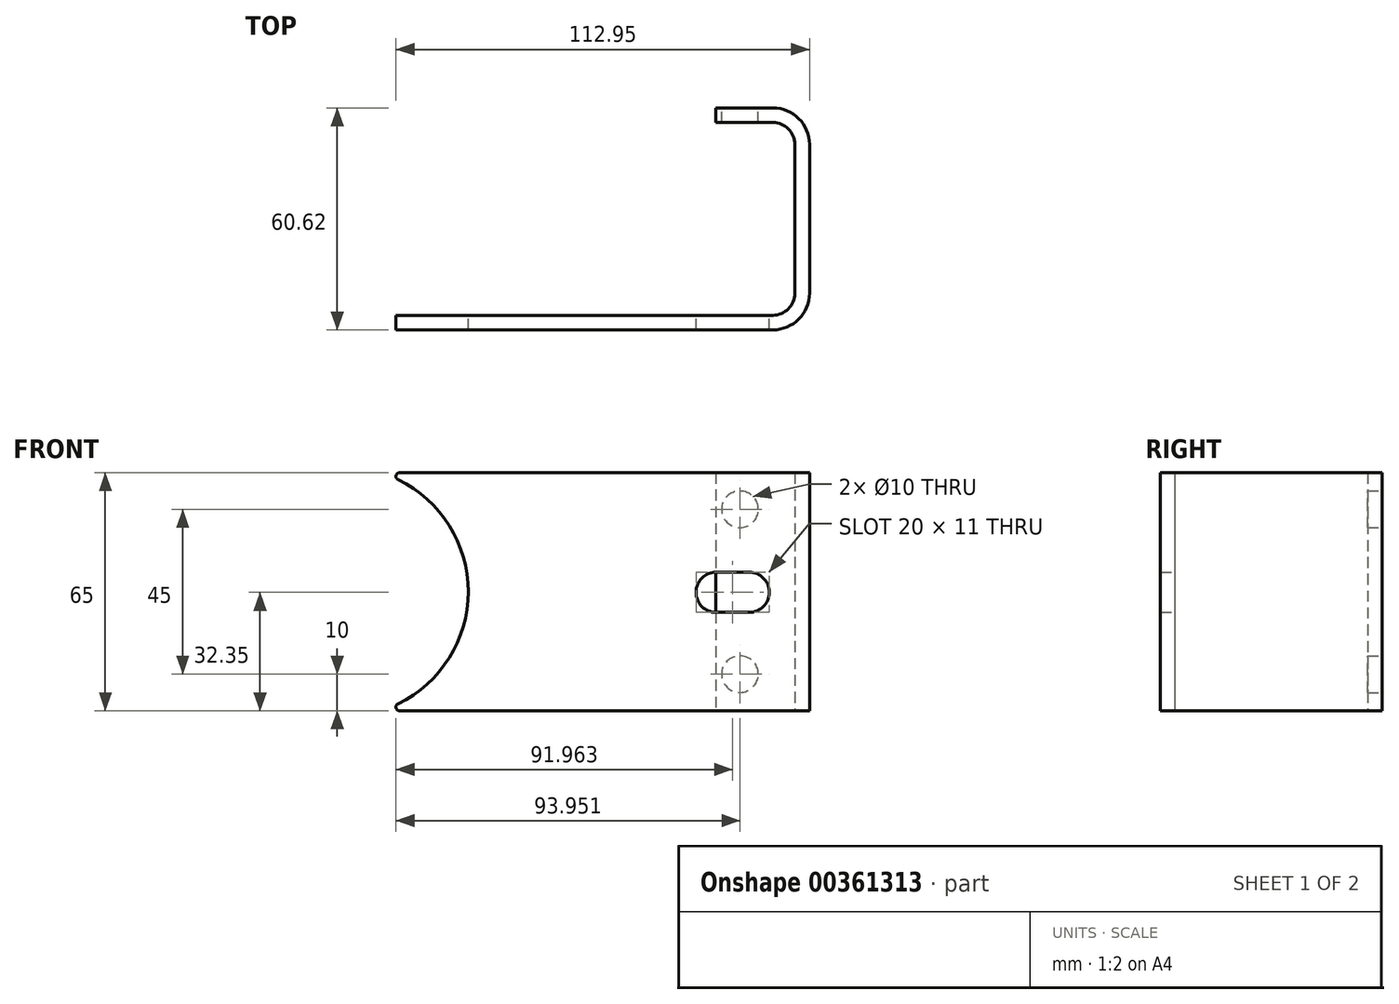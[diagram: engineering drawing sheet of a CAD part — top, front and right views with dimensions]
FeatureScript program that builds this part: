
annotation { "Feature Type Name" : "Feature", "Feature Type Description" : "" }
export const myFeature = defineFeature(function(context is Context, id is Id, definition is map)
    precondition{}
    {
        {
            var Q0;
            Q0=qCreatedBy(makeId("Top.planeOp"),FACE);
            var sketch = newSketch(context, id + "F0", { "sketchPlane" : qUnion([Q0])});
            skLineSegment(sketch, "E0", {"start": v(-71.16, -45.14) * mm, "end": v(45.97, -45.14) * mm});
            skLineSegment(sketch, "E1", {"start": v(55.97, -35.14) * mm, "end": v(55.97, 5.48) * mm});
            skLineSegment(sketch, "E2", {"start": v(45.97, 15.48) * mm, "end": v(30.35, 15.48) * mm});
            skLineSegment(sketch, "E3", {"start": v(30.35, 15.48) * mm, "end": v(30.35, 11.48) * mm});
            skLineSegment(sketch, "E4", {"start": v(30.35, 11.48) * mm, "end": v(45.97, 11.48) * mm});
            skLineSegment(sketch, "E5", {"start": v(51.97, 5.48) * mm, "end": v(51.97, -35.14) * mm});
            skLineSegment(sketch, "E6", {"start": v(45.97, -41.14) * mm, "end": v(-71.16, -41.14) * mm});
            skLineSegment(sketch, "E7", {"start": v(-71.16, -41.14) * mm, "end": v(-71.16, -45.14) * mm});
            skPoint(sketch, "E8.visualSharp", {"position": v(55.97, 15.48) * mm});
            skArc(sketch, "E8.filletArc", {"start": v(55.97, 5.48) * mm, "mid": v(53.04, 12.55) * mm, "end": v(45.97, 15.48) * mm});
            skPoint(sketch, "E9.visualSharp", {"position": v(55.97, -45.14) * mm});
            skArc(sketch, "E9.filletArc", {"start": v(45.97, -45.14) * mm, "mid": v(53.04, -42.21) * mm, "end": v(55.97, -35.14) * mm});
            skPoint(sketch, "E10.visualSharp", {"position": v(51.97, 11.48) * mm});
            skArc(sketch, "E10.filletArc", {"start": v(51.97, 5.48) * mm, "mid": v(50.21, 9.72) * mm, "end": v(45.97, 11.48) * mm});
            skPoint(sketch, "E11.visualSharp", {"position": v(51.97, -41.14) * mm});
            skArc(sketch, "E11.filletArc", {"start": v(45.97, -41.14) * mm, "mid": v(50.21, -39.38) * mm, "end": v(51.97, -35.14) * mm});
            skSolve(sketch);
        }
        {
            var Q0;
            Q0=makeQuery(id+"F0.imprint","IMPRINT",FACE,{"disambiguationData":[TD([[makeQuery(id+"F0.imprint","IMPRINT",EDGE,{"derivedFrom":sQuery(id+"F0.wireOp",EDGE,"E0")}),1.0]])]});
            extrude(context, id + "F1", {"entities" : qUnion([Q0]), "depth" : 65 * mm});
        }
        {
            var Q0;
            Q0=makeQuery(id+"F1.opExtrude","SWEPT_FACE",FACE,{"disambiguationData":[OSD([sQuery(id+"F0.wireOp",EDGE,"E2")])]});
            var sketch = newSketch(context, id + "F2", { "sketchPlane" : qUnion([Q0])});
            skSolve(sketch);
        }
        {
            var Q0;
            {var subQ0=sQuery(id+"F0.wireOp",EDGE,"E2");Q0=makeQuery(id+"F2.imprint","IMPRINT",FACE,{"disambiguationData":[TD([[makeQuery(id+"F2.imprint","IMPRINT",EDGE,{"derivedFrom":makeQuery(id+"F1.opExtrude","CAP_EDGE",EDGE,{"disambiguationData":[OSD([subQ0])],"isStart":true})}),1.0]])]});}
            var sketch = newSketch(context, id + "F3", { "sketchPlane" : qUnion([Q0])});
            skCircle(sketch, "E12", {"center": v(-36.97, 10) * mm, "radius": 5 * mm});
            skCircle(sketch, "E13", {"center": v(-36.97, 55) * mm, "radius": 5 * mm});
            skSolve(sketch);
        }
        {
            var Q0;
            Q0 = qSketchRegion(id + "F3", true);
            extrude(context, id + "F4", {"entities" : qUnion([Q0]), "operationType" : NewBodyOperationType.REMOVE, "oppositeDirection" : true, "depth" : 4 * mm});
        }
        {
            var Q0;
            Q0=makeQuery(id+"F1.opExtrude","SWEPT_FACE",FACE,{"disambiguationData":[OSD([sQuery(id+"F0.wireOp",EDGE,"E6")])]});
            var sketch = newSketch(context, id + "F5", { "sketchPlane" : qUnion([Q0])});
            skSolve(sketch);
        }
        {
            var Q0;
            {var subQ0=sQuery(id+"F0.wireOp",EDGE,"E6");Q0=makeQuery(id+"F5.imprint","IMPRINT",FACE,{"disambiguationData":[TD([[makeQuery(id+"F5.imprint","IMPRINT",EDGE,{"derivedFrom":makeQuery(id+"F1.opExtrude","CAP_EDGE",EDGE,{"disambiguationData":[OSD([subQ0])],"isStart":true})}),1.0]])]});}
            var sketch = newSketch(context, id + "F6", { "sketchPlane" : qUnion([Q0])});
            skArc(sketch, "E14", {"start": v(61.36, 65.03) * mm, "mid": v(37.24, 32.5) * mm, "end": v(61.36, -0.03) * mm});
            skPoint(sketch, "E15", {"position": v(61.36, -0.03) * mm});
            skPoint(sketch, "E16", {"position": v(61.36, 65.03) * mm});
            skLineSegment(sketch, "E17", {"start": v(61.36, -0.03) * mm, "end": v(78.91, -0.03) * mm});
            skLineSegment(sketch, "E18", {"start": v(78.91, -0.03) * mm, "end": v(78.91, 65.03) * mm});
            skLineSegment(sketch, "E19", {"start": v(78.91, 65.03) * mm, "end": v(61.36, 65.03) * mm});
            skSolve(sketch);
        }
        {
            var Q0;
            Q0 = qSketchRegion(id + "F6", true);
            extrude(context, id + "F7", {"entities" : qUnion([Q0]), "operationType" : NewBodyOperationType.REMOVE, "oppositeDirection" : true, "depth" : 25 * mm});
        }
        {
            var Q0;
            Q0=makeQuery(id+"F7.boolean.opBoolean","INTERSECT",EDGE,{"derivedFrom":[makeQuery(id+"F1.opExtrude","CAP_FACE",FACE,{"disambiguationData":[OSD([sQuery(id+"F0.wireOp",EDGE,"E0"),sQuery(id+"F0.wireOp",EDGE,"E1"),sQuery(id+"F0.wireOp",EDGE,"E2"),sQuery(id+"F0.wireOp",EDGE,"E3"),sQuery(id+"F0.wireOp",EDGE,"E4"),sQuery(id+"F0.wireOp",EDGE,"E5"),sQuery(id+"F0.wireOp",EDGE,"E6"),sQuery(id+"F0.wireOp",EDGE,"E7"),sQuery(id+"F0.wireOp",EDGE,"E8.filletArc"),sQuery(id+"F0.wireOp",EDGE,"E9.filletArc"),sQuery(id+"F0.wireOp",EDGE,"E10.filletArc"),sQuery(id+"F0.wireOp",EDGE,"E11.filletArc")])],"isStart":false}),makeQuery(id+"F7.opExtrude","SWEPT_FACE",FACE,{"disambiguationData":[OSD([sQuery(id+"F6.wireOp",EDGE,"E14")])]})]});
            var Q1;
            Q1=makeQuery(id+"F7.boolean.opBoolean","INTERSECT",EDGE,{"derivedFrom":[makeQuery(id+"F1.opExtrude","CAP_FACE",FACE,{"disambiguationData":[OSD([sQuery(id+"F0.wireOp",EDGE,"E0"),sQuery(id+"F0.wireOp",EDGE,"E1"),sQuery(id+"F0.wireOp",EDGE,"E2"),sQuery(id+"F0.wireOp",EDGE,"E3"),sQuery(id+"F0.wireOp",EDGE,"E4"),sQuery(id+"F0.wireOp",EDGE,"E5"),sQuery(id+"F0.wireOp",EDGE,"E6"),sQuery(id+"F0.wireOp",EDGE,"E7"),sQuery(id+"F0.wireOp",EDGE,"E8.filletArc"),sQuery(id+"F0.wireOp",EDGE,"E9.filletArc"),sQuery(id+"F0.wireOp",EDGE,"E10.filletArc"),sQuery(id+"F0.wireOp",EDGE,"E11.filletArc")])],"isStart":true}),makeQuery(id+"F7.opExtrude","SWEPT_FACE",FACE,{"disambiguationData":[OSD([sQuery(id+"F6.wireOp",EDGE,"E14")])]})]});
            fillet(context, id + "F8", {"entities" : qUnion([Q0, Q1]), "radius" : 1 * mm, "tangentPropagation" : true, "allowEdgeOverflow" : false});
        }
        {
            var Q0;
            {var subQ0=sQuery(id+"F0.wireOp",EDGE,"E6");Q0=makeQuery(id+"F5.imprint","IMPRINT",FACE,{"disambiguationData":[TD([[makeQuery(id+"F5.imprint","IMPRINT",EDGE,{"derivedFrom":makeQuery(id+"F1.opExtrude","CAP_EDGE",EDGE,{"disambiguationData":[OSD([subQ0])],"isStart":true})}),1.0]])]});}
            var sketch = newSketch(context, id + "F9", { "sketchPlane" : qUnion([Q0])});
            skArc(sketch, "E20", {"start": v(-30.48, 26.85) * mm, "mid": v(-24.98, 32.35) * mm, "end": v(-30.48, 37.85) * mm});
            skLineSegment(sketch, "E21", {"start": v(-30.48, 26.85) * mm, "end": v(-39.48, 26.85) * mm});
            skLineSegment(sketch, "E22", {"start": v(-30.48, 37.85) * mm, "end": v(-39.48, 37.85) * mm});
            skArc(sketch, "E23", {"start": v(-39.48, 37.85) * mm, "mid": v(-44.98, 32.35) * mm, "end": v(-39.48, 26.85) * mm});
            skSolve(sketch);
        }
        {
            var Q0;
            Q0 = qSketchRegion(id + "F9", true);
            extrude(context, id + "F10", {"entities" : qUnion([Q0]), "operationType" : NewBodyOperationType.REMOVE, "endBound" : BoundingType.THROUGH_ALL, "oppositeDirection" : true, "depth" : 25 * mm});
        }
    });
